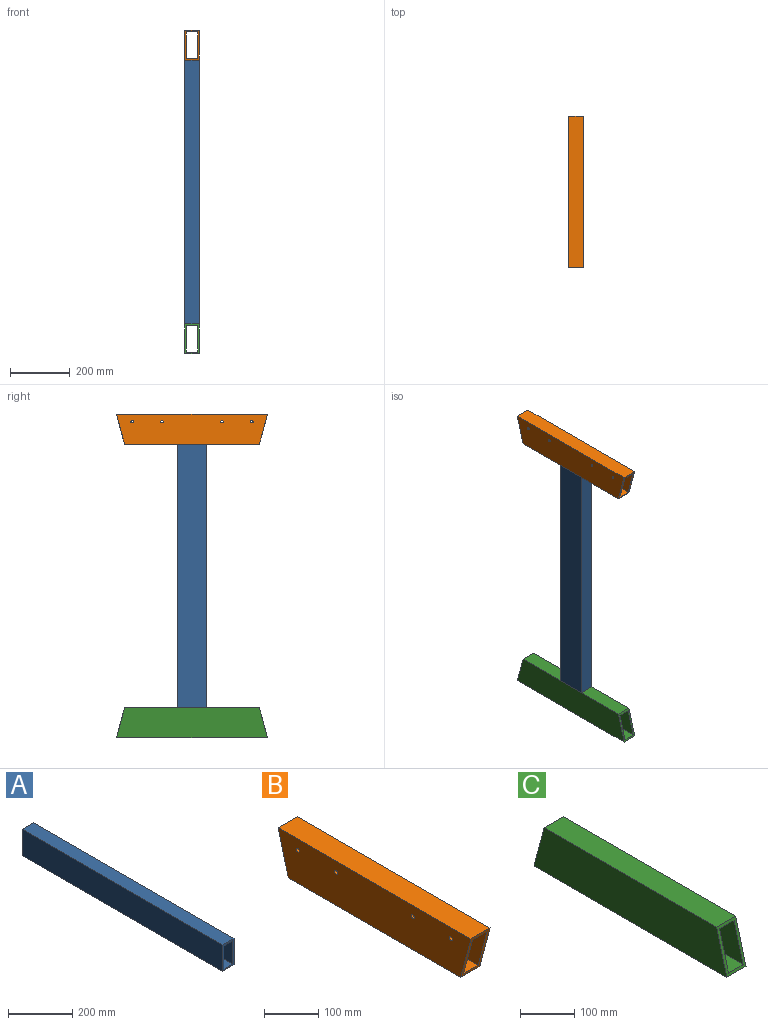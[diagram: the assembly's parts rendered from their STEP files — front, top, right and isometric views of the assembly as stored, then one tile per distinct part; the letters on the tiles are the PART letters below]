
ASSEMBLY  parts=3 mates=2
PART A: 10 faces, bbox 50x880x100 mm
  f0: plane 880x88mm, normal (1,0,0), area 77440mm2, adj f1,f7,f8,f9
  f1: plane 880x38mm, normal (0,0,-1), area 33440mm2, adj f0,f2,f8,f9
  f2: plane 880x88mm, normal (-1,0,0), area 77440mm2, adj f1,f7,f8,f9
  f3: plane 880x100mm, normal (-1,0,0), area 88000mm2, adj f4,f6,f8,f9
  f4: plane 880x50mm, normal (0,0,-1), area 44000mm2, adj f3,f5,f8,f9
  f5: plane 880x100mm, normal (1,0,0), area 88000mm2, adj f4,f6,f8,f9
  f6: plane 880x50mm, normal (0,0,1), area 44000mm2, adj f3,f5,f8,f9
  f7: plane 880x38mm, normal (0,0,1), area 33440mm2, adj f0,f2,f8,f9
  f8: plane 100x50mm, normal (0,-1,0), area 1656mm2, adj f0,f1,f2,f3,f4,f5,f6,f7
  f9: plane 100x50mm, normal (0,1,0), area 1656mm2, adj f0,f1,f2,f3,f4,f5,f6,f7
PART B: 18 faces, bbox 50x503.6x100 mm
  f0: plane 503.59x50mm, normal (0,0,1), area 25179.5mm2, adj f6,f7,f12,f13
  f1: plane 500.37x88mm, normal (1,0,0), area 41756.9mm2, adj f2,f5,f12,f13,f14,f15,f16,f17
  f2: plane 500.37x38mm, normal (0,0,-1), area 19014.2mm2, adj f1,f3,f12,f13
  f3: plane 500.37x88mm, normal (-1,0,0), area 41756.9mm2, adj f2,f5,f8,f9,f10,f11,f12,f13
  f4: plane 450x50mm, normal (0,0,-1), area 22500mm2, adj f6,f7,f12,f13
  f5: plane 453.22x38mm, normal (0,0,1), area 17222.2mm2, adj f1,f3,f12,f13
  f6: plane 503.59x100mm, normal (-1,0,0), area 47478.4mm2, adj f0,f4,f12,f13,f14,f15,f16,f17
  f7: plane 503.59x100mm, normal (1,0,0), area 47478.4mm2, adj f0,f4,f8,f9,f10,f11,f12,f13
  f8: cylinder r=4mm len=8mm, axis (1,0,0), area 150.8mm2, adj f3,f7
  f9: cylinder r=4mm len=8mm, axis (1,0,0), area 150.8mm2, adj f3,f7
  f10: cylinder r=4mm len=8mm, axis (1,0,0), area 150.8mm2, adj f3,f7
  f11: cylinder r=4mm len=8mm, axis (1,0,0), area 150.8mm2, adj f3,f7
  f12: plane 100x50mm, normal (0,0.97,-0.26), area 1714.4mm2, adj f0,f1,f2,f3,f4,f5,f6,f7
  f13: plane 100x50mm, normal (0,-0.97,-0.26), area 1714.4mm2, adj f0,f1,f2,f3,f4,f5,f6,f7
  f14: cylinder r=4mm len=8mm, axis (1,0,0), area 150.8mm2, adj f1,f6
  f15: cylinder r=4mm len=8mm, axis (1,0,0), area 150.8mm2, adj f1,f6
  f16: cylinder r=4mm len=8mm, axis (1,0,0), area 150.8mm2, adj f1,f6
  f17: cylinder r=4mm len=8mm, axis (1,0,0), area 150.8mm2, adj f1,f6
PART C: 10 faces, bbox 50x503.6x100 mm
  f0: plane 500.37x38mm, normal (0,0,1), area 19014.2mm2, adj f1,f3,f4,f5
  f1: plane 500.37x88mm, normal (-1,0,0), area 41958mm2, adj f0,f2,f4,f5
  f2: plane 453.22x38mm, normal (0,0,-1), area 17222.2mm2, adj f1,f3,f4,f5
  f3: plane 500.37x88mm, normal (1,0,0), area 41958mm2, adj f0,f2,f4,f5
  f4: plane 100x50mm, normal (0,0.97,0.26), area 1714.4mm2, adj f0,f1,f2,f3,f6,f7,f8,f9
  f5: plane 100x50mm, normal (0,-0.97,0.26), area 1714.4mm2, adj f0,f1,f2,f3,f6,f7,f8,f9
  f6: plane 503.59x100mm, normal (-1,0,0), area 47679.5mm2, adj f4,f5,f7,f9
  f7: plane 503.59x50mm, normal (0,0,-1), area 25179.5mm2, adj f4,f5,f6,f8
  f8: plane 503.59x100mm, normal (1,0,0), area 47679.5mm2, adj f4,f5,f7,f9
  f9: plane 450x50mm, normal (0,0,1), area 22500mm2, adj f4,f5,f6,f8
PLACE A rot(axis=(1,0,0),90deg) t=(-25,50,980)mm
PLACE B t=(-25,255,980)mm
PLACE C t=(-25,255,0)mm
MATE fastened C.f9 <-> A.f8  axis (0,0,1) through (0,0,100)mm
MATE fastened A.f9 <-> B.f4  axis (0,0,1) through (0,0,980)mm
